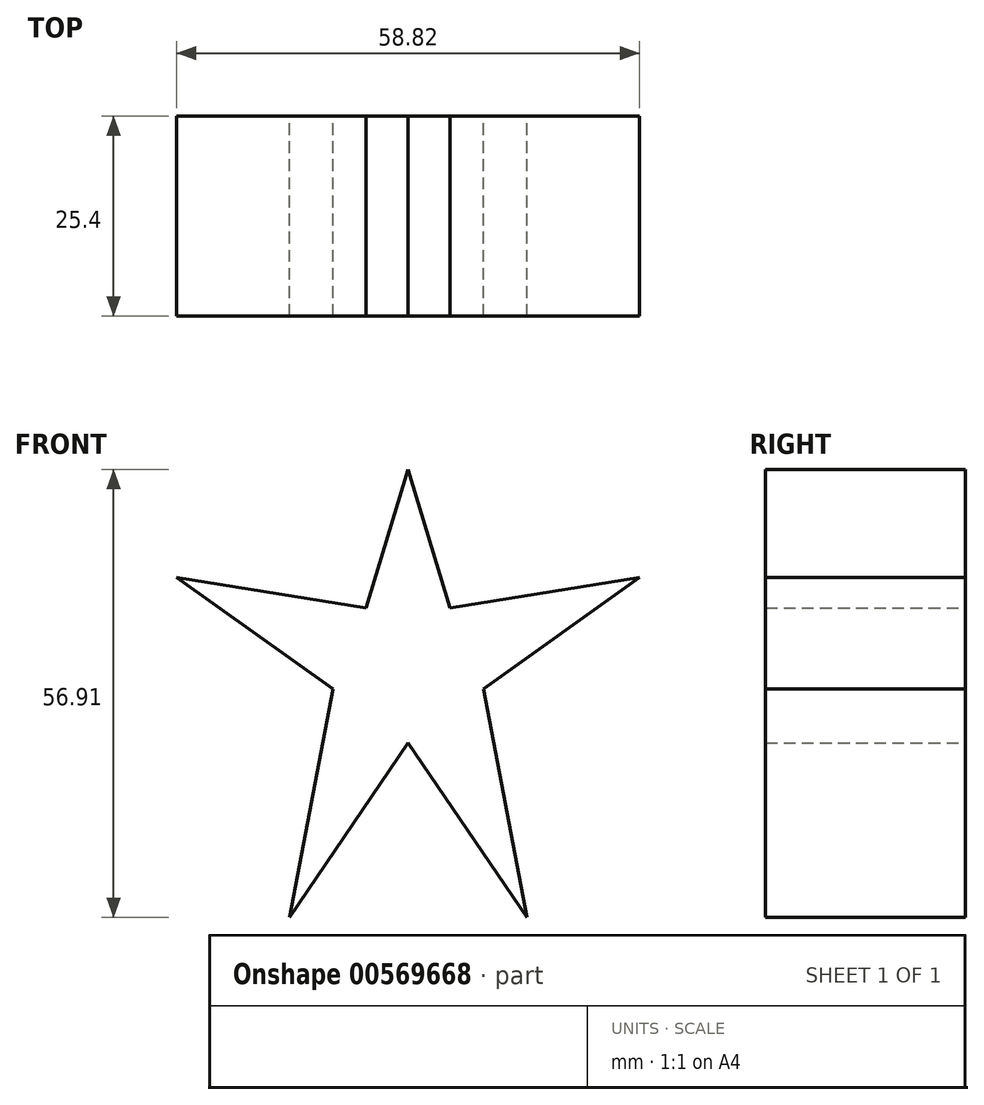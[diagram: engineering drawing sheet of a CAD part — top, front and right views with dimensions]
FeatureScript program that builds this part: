
annotation { "Feature Type Name" : "Feature", "Feature Type Description" : "" }
export const myFeature = defineFeature(function(context is Context, id is Id, definition is map)
    precondition{}
    {
        {
            var Q0;
            Q0=qCreatedBy(makeId("Front.planeOp"),FACE);
            var sketch = newSketch(context, id + "F0", { "sketchPlane" : qUnion([Q0])});
            skLineSegment(sketch, "E0.bottom", {"start": v(55.95, 55.95) * mm, "end": v(-57.29, 55.95) * mm});
            skLineSegment(sketch, "E0.top", {"start": v(55.95, -55.57) * mm, "end": v(-57.29, -55.57) * mm});
            skLineSegment(sketch, "E0.left", {"start": v(55.95, 55.95) * mm, "end": v(55.95, -55.57) * mm});
            skLineSegment(sketch, "E0.right", {"start": v(-57.29, 55.95) * mm, "end": v(-57.29, -55.57) * mm});
            skPoint(sketch, "E1", {"position": v(-0.67, 55.95) * mm});
            skPoint(sketch, "E2", {"position": v(29.22, -55.57) * mm});
            skPoint(sketch, "E3", {"position": v(-57.29, 19.67) * mm});
            skPoint(sketch, "E4", {"position": v(55.95, 19.67) * mm});
            skLineSegment(sketch, "E5", {"start": v(15.09, -29.03) * mm, "end": v(9.55, 0) * mm});
            skLineSegment(sketch, "E6", {"start": v(9.55, 0) * mm, "end": v(29.4, 14.13) * mm});
            skLineSegment(sketch, "E7", {"start": v(29.4, 14.13) * mm, "end": v(5.35, 10.31) * mm});
            skLineSegment(sketch, "E8", {"start": v(5.35, 10.31) * mm, "end": v(0, 27.88) * mm});
            skLineSegment(sketch, "E9", {"start": v(15.09, -29.03) * mm, "end": v(0, -6.87) * mm});
            skLineSegment(sketch, "E10", {"start": v(0, -6.87) * mm, "end": v(0, 27.88) * mm});
            skCircle(sketch, "E11.cCircle", {"center": v(-122.97, 2.3) * mm, "radius": 13.83 * mm, "construction": true});
            skLineSegment(sketch, "E11.0", {"start": v(-110.56, 8.4) * mm, "end": v(-113.33, -7.62) * mm});
            skLineSegment(sketch, "E11.1", {"start": v(-113.33, -7.62) * mm, "end": v(-129.42, -9.95) * mm});
            skLineSegment(sketch, "E11.2", {"start": v(-129.42, -9.95) * mm, "end": v(-136.6, 4.64) * mm});
            skLineSegment(sketch, "E11.3", {"start": v(-136.6, 4.64) * mm, "end": v(-124.95, 15.98) * mm});
            skLineSegment(sketch, "E11.4", {"start": v(-124.95, 15.98) * mm, "end": v(-110.56, 8.4) * mm});
            skSolve(sketch);
        }
        {
            var Q0;
            Q0=makeQuery(id+"F0.imprint","IMPRINT",FACE,{"disambiguationData":[TD([[makeQuery(id+"F0.imprint","IMPRINT",EDGE,{"derivedFrom":sQuery(id+"F0.wireOp",EDGE,"E5")}),1.0]])]});
            extrude(context, id + "F1", {"entities" : qUnion([Q0]), "depth" : 25.4 * mm, "offsetDistance" : 25.4 * mm});
        }
        {
            var Q0;
            Q0=makeQuery(id+"F1.opExtrude","SWEPT_BODY",BODY,{"disambiguationData":[OSD([sQuery(id+"F0.wireOp",EDGE,"E5"),sQuery(id+"F0.wireOp",EDGE,"E6"),sQuery(id+"F0.wireOp",EDGE,"E7"),sQuery(id+"F0.wireOp",EDGE,"E8"),sQuery(id+"F0.wireOp",EDGE,"E9"),sQuery(id+"F0.wireOp",EDGE,"E10")])]});
            var Q1;
            Q1=qCreatedBy(makeId("Right.planeOp"),FACE);
            mirror(context, id + "F2", {"operationType" : NewBodyOperationType.ADD, "entities" : qUnion([Q0]), "mirrorPlane" : qUnion([Q1])});
        }
    });
